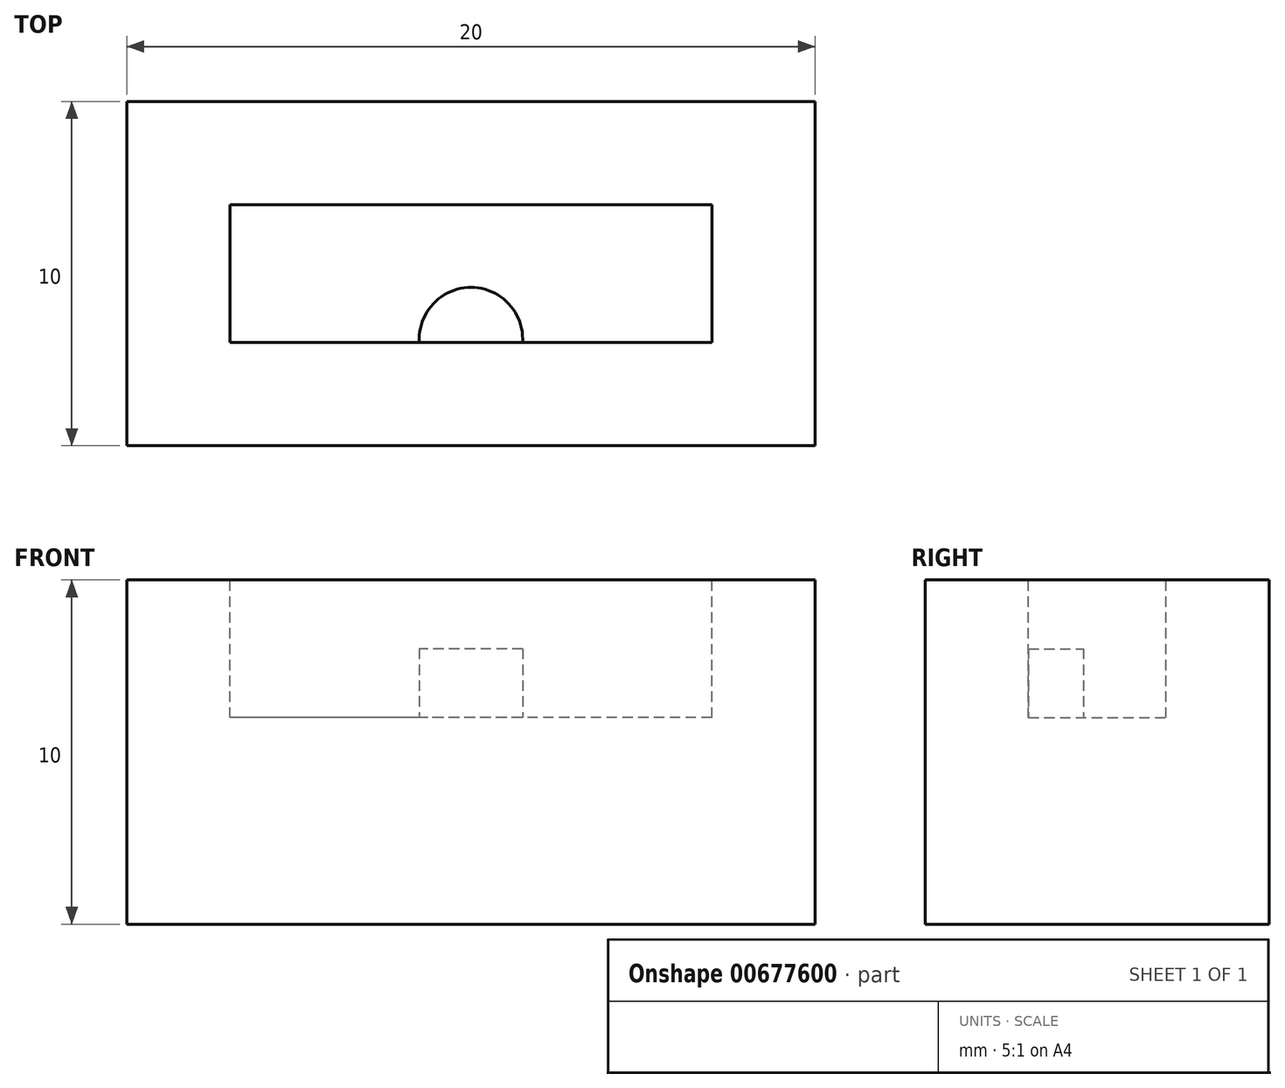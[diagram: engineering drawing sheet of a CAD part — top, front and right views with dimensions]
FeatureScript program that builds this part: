
annotation { "Feature Type Name" : "Feature", "Feature Type Description" : "" }
export const myFeature = defineFeature(function(context is Context, id is Id, definition is map)
    precondition{}
    {
        {
            var Q0;
            Q0=qCreatedBy(makeId("Top.planeOp"),FACE);
            var sketch = newSketch(context, id + "F0", { "sketchPlane" : qUnion([Q0])});
            skLineSegment(sketch, "E0.bottom", {"start": v(10, -5) * mm, "end": v(-10, -5) * mm});
            skLineSegment(sketch, "E0.top", {"start": v(10, 5) * mm, "end": v(-10, 5) * mm});
            skLineSegment(sketch, "E0.left", {"start": v(10, -5) * mm, "end": v(10, 5) * mm});
            skLineSegment(sketch, "E0.right", {"start": v(-10, -5) * mm, "end": v(-10, 5) * mm});
            skPoint(sketch, "E0.middle", {"position": v(0, 0) * mm});
            skSolve(sketch);
        }
        {
            var Q0;
            Q0 = qSketchRegion(id + "F0", true);
            extrude(context, id + "F1", {"entities" : qUnion([Q0]), "depth" : 10 * mm, "offsetDistance" : 25 * mm});
        }
        {
            var Q0;
            Q0=makeQuery(id+"F1.opExtrude","CAP_FACE",FACE,{"disambiguationData":[OSD([sQuery(id+"F0.wireOp",EDGE,"E0.bottom"),sQuery(id+"F0.wireOp",EDGE,"E0.top"),sQuery(id+"F0.wireOp",EDGE,"E0.left"),sQuery(id+"F0.wireOp",EDGE,"E0.right")])],"isStart":false});
            var sketch = newSketch(context, id + "F2", { "sketchPlane" : qUnion([Q0])});
            skLineSegment(sketch, "E1.bottom", {"start": v(7, -2) * mm, "end": v(-7, -2) * mm});
            skLineSegment(sketch, "E1.top", {"start": v(7, 2) * mm, "end": v(-7, 2) * mm});
            skLineSegment(sketch, "E1.left", {"start": v(7, -2) * mm, "end": v(7, 2) * mm});
            skLineSegment(sketch, "E1.right", {"start": v(-7, -2) * mm, "end": v(-7, 2) * mm});
            skPoint(sketch, "E1.middle", {"position": v(0, 0) * mm});
            skSolve(sketch);
        }
        {
            var Q0;
            Q0 = qSketchRegion(id + "F2", true);
            extrude(context, id + "F3", {"entities" : qUnion([Q0]), "operationType" : NewBodyOperationType.REMOVE, "oppositeDirection" : true, "depth" : 4 * mm, "offsetDistance" : 25 * mm});
        }
        {
            var Q0;
            Q0=makeQuery(id+"F3.boolean.opBoolean","COPY",FACE,{"derivedFrom":makeQuery(id+"F3.opExtrude","CAP_FACE",FACE,{"disambiguationData":[OSD([sQuery(id+"F2.wireOp",EDGE,"E1.bottom"),sQuery(id+"F2.wireOp",EDGE,"E1.top"),sQuery(id+"F2.wireOp",EDGE,"E1.left"),sQuery(id+"F2.wireOp",EDGE,"E1.right")])],"isStart":false})});
            var sketch = newSketch(context, id + "F4", { "sketchPlane" : qUnion([Q0])});
            skPoint(sketch, "E2", {"position": v(-1.5, -2) * mm});
            skPoint(sketch, "E3", {"position": v(1.5, -2) * mm});
            skPoint(sketch, "E4", {"position": v(0, -0.4) * mm});
            skArc(sketch, "E5", {"start": v(1.5, -2) * mm, "mid": v(0, -0.4) * mm, "end": v(-1.5, -2) * mm});
            skSolve(sketch);
        }
        {
            var Q0;
            {var subQ0=sQuery(id+"F4.wireOp",EDGE,"E5");Q0=makeQuery(id+"F4.imprint","IMPRINT",FACE,{"disambiguationData":[TD([[makeQuery(id+"F4.imprint","IMPRINT",EDGE,{"derivedFrom":subQ0}),1.0]])]});}
            extrude(context, id + "F5", {"entities" : qUnion([Q0]), "operationType" : NewBodyOperationType.ADD, "depth" : 2 * mm, "offsetDistance" : 25 * mm});
        }
    });
